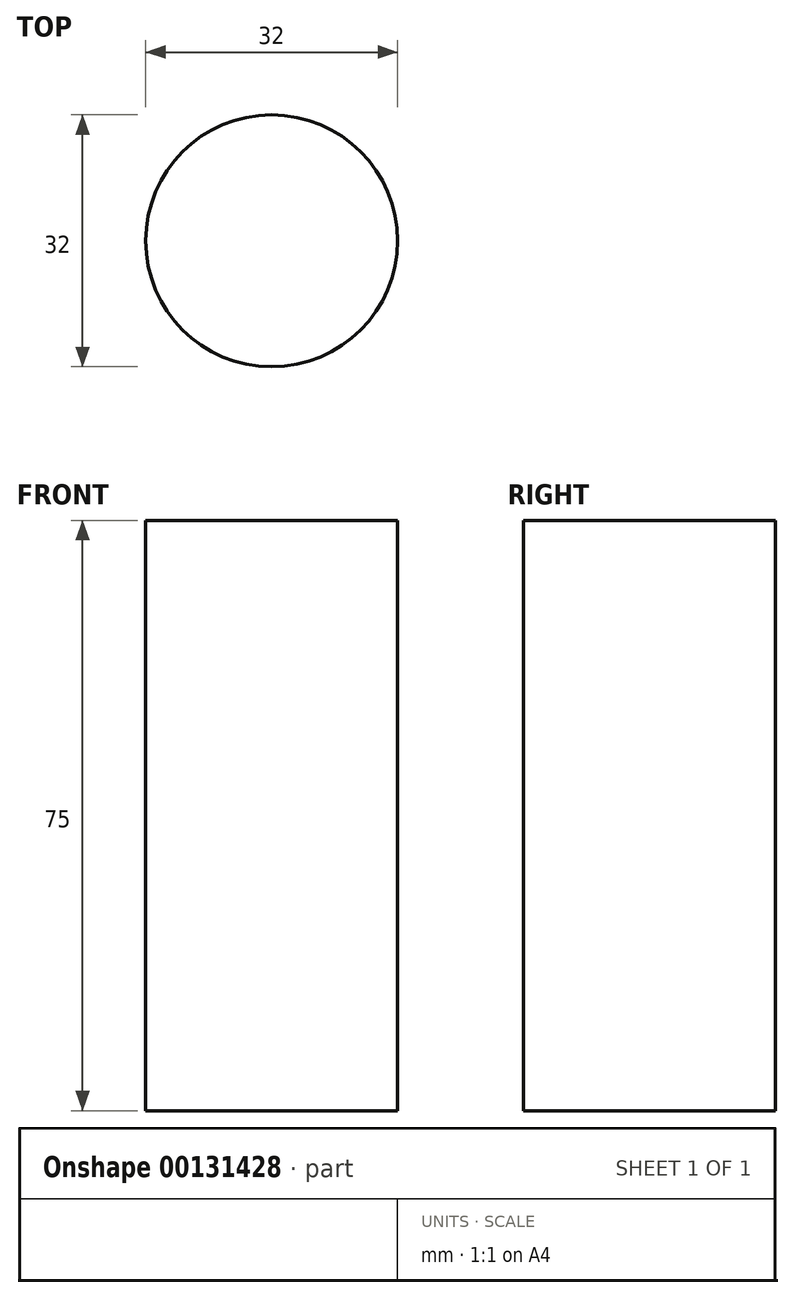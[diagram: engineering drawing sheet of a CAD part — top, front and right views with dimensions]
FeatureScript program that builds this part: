
annotation { "Feature Type Name" : "Feature", "Feature Type Description" : "" }
export const myFeature = defineFeature(function(context is Context, id is Id, definition is map)
    precondition{}
    {
        {
            var Q0;
            Q0=qCreatedBy(makeId("Top.planeOp"),FACE);
            var sketch = newSketch(context, id + "F0", { "sketchPlane" : qUnion([Q0])});
            skCircle(sketch, "E0", {"center": v(0, 0) * mm, "radius": 16 * mm});
            skSolve(sketch);
        }
        {
            var Q0;
            Q0=makeQuery(id+"F0.imprint","IMPRINT",FACE,{"disambiguationData":[TD([[makeQuery(id+"F0.imprint","IMPRINT",EDGE,{"derivedFrom":sQuery(id+"F0.wireOp",EDGE,"E0")}),1.0]])]});
            extrude(context, id + "F1", {"entities" : qUnion([Q0]), "depth" : 75 * mm});
        }
    });
